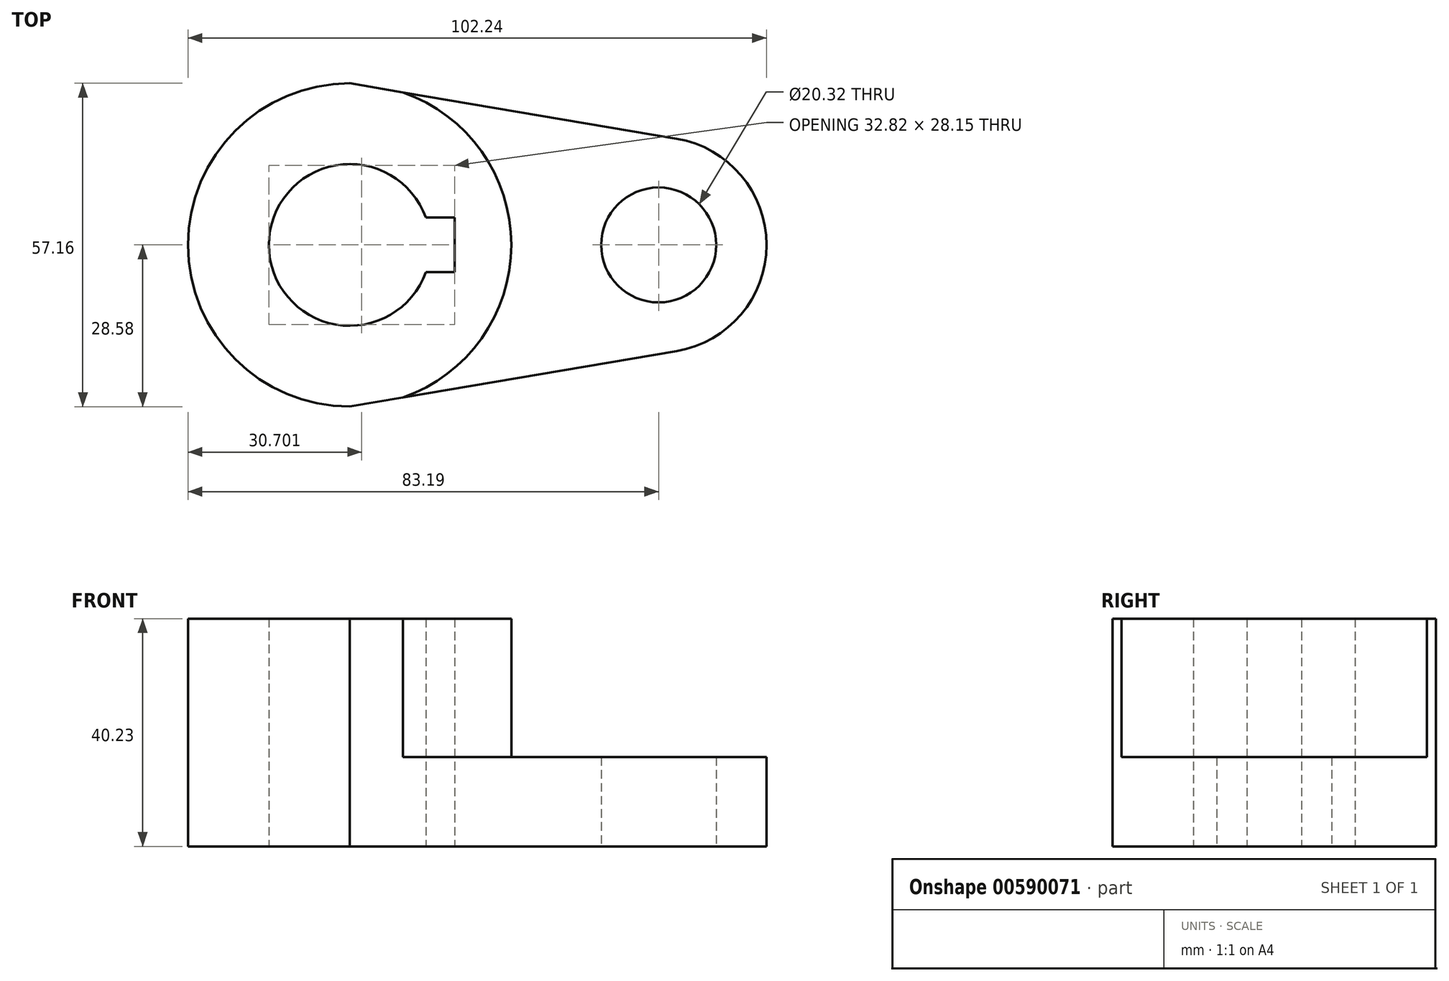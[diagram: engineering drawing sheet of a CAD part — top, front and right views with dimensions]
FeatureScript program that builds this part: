
annotation { "Feature Type Name" : "Feature", "Feature Type Description" : "" }
export const myFeature = defineFeature(function(context is Context, id is Id, definition is map)
    precondition{}
    {
        {
            var Q0;
            Q0=qCreatedBy(makeId("Top.planeOp"),FACE);
            var sketch = newSketch(context, id + "F0", { "sketchPlane" : qUnion([Q0])});
            skCircle(sketch, "E0", {"center": v(0, 0) * mm, "radius": 28.58 * mm});
            skArc(sketch, "E1", {"start": v(57.8, -18.78) * mm, "mid": v(73.66, 0) * mm, "end": v(57.8, 18.78) * mm});
            skLineSegment(sketch, "E2", {"start": v(0, 28.58) * mm, "end": v(57.8, 18.78) * mm});
            skLineSegment(sketch, "E3", {"start": v(0, -28.58) * mm, "end": v(57.8, -18.78) * mm});
            skCircle(sketch, "E4", {"center": v(54.61, 0) * mm, "radius": 10.16 * mm});
            skArc(sketch, "E5", {"start": v(13.45, 4.83) * mm, "mid": v(-14.29, 0) * mm, "end": v(13.45, -4.83) * mm});
            skLineSegment(sketch, "E6.bottom", {"start": v(18.53, 4.83) * mm, "end": v(13.45, 4.83) * mm});
            skLineSegment(sketch, "E6.top", {"start": v(18.53, -4.83) * mm, "end": v(13.45, -4.83) * mm});
            skLineSegment(sketch, "E6.left", {"start": v(18.53, 4.83) * mm, "end": v(18.53, -4.83) * mm});
            skLineSegment(sketch, "E7", {"start": v(18.53, 0) * mm, "end": v(0, 0) * mm, "construction": true});
            skSolve(sketch);
        }
        {
            var Q0;
            {var subQ1=sQuery(id+"F0.wireOp",EDGE,"E1");Q0=makeQuery(id+"F0.imprint","IMPRINT",FACE,{"disambiguationData":[TD([[makeQuery(id+"F0.imprint","IMPRINT",EDGE,{"derivedFrom":subQ1}),1.0]])]});}
            extrude(context, id + "F1", {"entities" : qUnion([Q0]), "depth" : 15.77 * mm, "offsetDistance" : 25.4 * mm});
        }
        {
            var Q0;
            Q0=makeQuery(id+"F0.imprint","IMPRINT",FACE,{"disambiguationData":[TD([[makeQuery(id+"F0.imprint","IMPRINT",EDGE,{"derivedFrom":sQuery(id+"F0.wireOp",EDGE,"E5")}),-1.0]])]});
            extrude(context, id + "F2", {"entities" : qUnion([Q0]), "operationType" : NewBodyOperationType.ADD, "depth" : 40.23 * mm, "offsetDistance" : 25.4 * mm});
        }
    });
